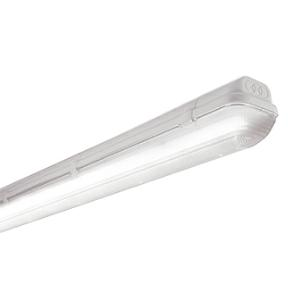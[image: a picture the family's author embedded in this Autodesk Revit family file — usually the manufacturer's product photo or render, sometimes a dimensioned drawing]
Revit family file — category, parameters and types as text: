
# Revit family: 3f_filippi_-_3f_linda_basic_3f_filippi_-_58766_-_3f_linda_led_basic_st_2x16w_l1270
name_source: partatom
category: Lighting Fixtures
units: mm (PartAtom-declared; Revit-internal decimal feet)

## family parameters
Cut with Voids When Loaded = No
Host = Face
Light Source = No
Part Type = Normal
Room Calculation Point = No
Round Connector Dimension = Use Diameter
Shared = No

## types (1)
- 3F Filippi - 3F Linda Basic (1 x LED, 4711 lm, 31 W, 4000 K)
    Apparent Load = 31 VA
    Approval mark = CE
    CIE Flux Codes = 43 74 92 95 100
    Color Rendering = 80
    Color Temperature = 4000 K
    Control Gear = Electronic ballast
    Default Elevation = 1800 mm
    Description = ILLUMINOTECHNICAL
Luminous efficiency 100% (DLOR 95%, ULOR 5%).
Initial luminous flux of the luminaire 4711 lm.
Controlled symmetric distribution.
Installation Interdistance Transv.D = 1.05 x hu - Long.D = 1.20 x hu.
Tabular UGR (CIE 117 - 4H-8H; S=0.25H; 70/50/20): RUG 23.6 - 21.8.
Beam angle: 127° - 100°.
Luminous efficacy 152 lm/W.
Lifetime (L92/B10): 30000 h. (tq+25°C)
Lifetime (L85/B10): 50000 h. (tq+25°C)
Lifetime (L75/B10): 80000 h. (tq+25°C)
Lifetime (L70/B10): 100000 h. (tq+25°C)
Lifetime (L75/B10): 50000 h. (tq+35°C)
Sudden decreased luminous flux after 50000 hours: 0% (C0).
Photobiological safety in compliance with IEC/TR 62778: RG0 risk exempt, (IEC 62471).
In compliance with IEC/EN 62722-2-1 - IEC/EN 62717 standards.

SOURCE
2 linear LED modules 16W/840.
Energy efficiency class (UE 2019/2020 - UE 2019/2015): D.
CIE 13.3 Colour rendering index: CRI >80 (R9 <50%).
IES TM-30 Fidelity Index: Rf = 84 Rg = 95.
CCT nominal colour temperature 4000 K.
Colour initial tolerance (MacAdam): SDCM 3.

MECHANICAL
Self-extinguishing V2 polycarbonate housing, injection moulded, RAL 7035 grey.
Ecologic anti-aging injected sealing gasket.
Diffuser in self-extinguishing V2 polycarbonate, photo-engraved interior, UV stabilised, injection moulded with smooth outer surface, tamper-proof opening.
Gear-holder reflector in hot-dip galvanised steel, painted with white polyester base.
Snug fit snap-lock clips for diffuser mounting, in polycarbonate.
Fixing brackets in stainless steel.
Possibility for technicians to access the interior of the luminaire.
CSI certificate for food-preparation environments.
Luminaire with limited surface temperature. - D - (EN 60598-2-24)
Dimensions: 1270x100 mm, height 100 mm. Weight 1.984 kg.
IP66 protection degree.
Mechanical strength to impacts IK10 (20 joule).
Glow-wire test resistance 850°C.

ELECTRICAL
Halogen Free electronic wiring 230V-50/60Hz, power factor 0.95, THD <25%, constant output current, SELV, class I, 1 driver.
Power of the luminaire 31 W.
ENEC - CE.
SAFE FLICKER: PstLM=<1 and SVM=<0.4 (IEC TR 61547-1 and IEC TR 63158), to ensure a more comfortable and safe light.
Luminaire compliant with EN 60598-2-22 for power supply from a centralised emergency system CPSS (Central Power Supply System), not incorporated in the luminaire - high risk areas excluded. The default power and flux are 100% in AC and 100% in DC.
Ambient temperature from -20°C to +35°C.
Temperature class T6 max 85°C.
Relative humidity UR: <85%.

INSTALLATION
Ceiling / Suspended / Wall.
All accessories dedicated to this product are available on the Catalog and on our website www.3F-Filippi.com.

APPLICATIONS
Suitable product for food production plants (HACCP), IFS (Food Version 6), BRC (GSFS Food Version 7).
Dry, dusty indoor environments, subject to occasional water splashes.
Virtually shatterproof polycarbonate compatibly with the fumes / atmospheres that compromise the elasticity of plastic materials.
Not suitable for installation on surfaces subject to important vibrations, exposed to weather conditions, on ropes or poles.
Suitable for illumination of public car parks and parking grounds referred to DIN 67528:2018-04.

WARNING
Fixture not suitable for cold stores with an ambient temperature <0°C and/or relative humidity >85%.
Luminaire designed for disposal/recycling at end-of-life.
Replaceable (LED only) light source by a professional. Replaceable control gear by a professional.
    Height = 100 mm  [stored 0.328084 ft]
    Lamp = 1 x LED
    Lamp Light Flux = 4711 lm
    Lamp Power = 31 W
    Lamp count = 1
    Length = 1270 mm
    Lifetime = 50000 h
    Luminous efficacy = 152 lm/W
    Manufacturer = 3F Filippi
    ModVariant = No
    Model = 3F Filippi - 58766 - 3F Linda LED Basic ST 2x16W L1270
    Mounting Place = Ceiling
    Mounting Type = Pendant
    Number of Poles = 1
    OnlyDefault = Yes
    Power Factor = 1
    Product Name = 3F Filippi - 3F Linda Basic
    Product group = pendant luminaire
    ProductGroupID = 9
    Protection Class = Protection class I
    Protection Degree = IP 66
    RLX_Detail_Level = 1
    RLX_Emergency_Light_Flux = 0 lm
    RLX_Emergency_Type = 0
    RLX_Emergency_Type_DB = No
    RlxData = <blob elided: 67773 chars, md5=4fd480df>
    Socket = socket
    Standby Power = 0 W
    System Light Flux = 4711 lm
    System Power = 31 W
    Type Comments = Product without accessories
    Type Image = 3ffilippi_3f_linda_led_basic_st_2x.jpg
    URL = http://relux.com
    VarID = ---
    Voltage = 0 V
    Weight = 0.00 kg
    Width = 100 mm  [stored 0.328084 ft]

note: [stored X ft] marks values corroborated as IEEE doubles in the binary element streams (Revit-internal decimal feet)

## geometry (parser evidence)
native form markers: Blend x4, Sweep x12
no freeform markers — native parametric forms only
